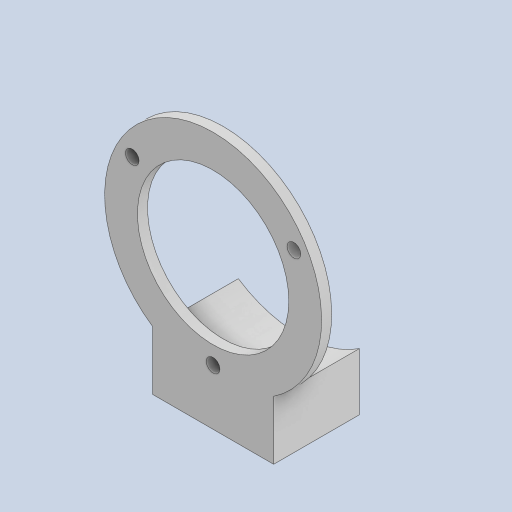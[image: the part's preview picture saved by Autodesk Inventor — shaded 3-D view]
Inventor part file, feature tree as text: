
AUTODESK INVENTOR PART (.ipt)
format: ipt  version: 2023 (Build 270158000, 158)  size: 240,128 bytes
history: native  units: mm
features: other x5, extrude x3, sketch x2, chamfer x1
ambient origin geometry x8: Origin, YZ Plane, XZ Plane, XY Plane, X Axis, Y Axis, Z Axis, Center Point
bodies: Body1 (feature_tree), Body2 (feature_tree)
feature tree (11):
  other  "GIM3505-8_with-driver.ipt"
  other  "ソリッド1"
  sketch  "スケッチ1"
  extrude  "押し出し1"  Depth=10.0mm
  extrude  "押し出し5"  Depth=2.7mm
  extrude  "押し出し6"  Depth=30.0mm TaperAngle=360.0deg
  chamfer  "面取り1"  Distance=30.0mm
  other  "TaggingFeature1"
  sketch  "スケッチ5"
  other  "ソリッド1::GIM3505-8_with-driver.ipt"
  other  "Srf1"
